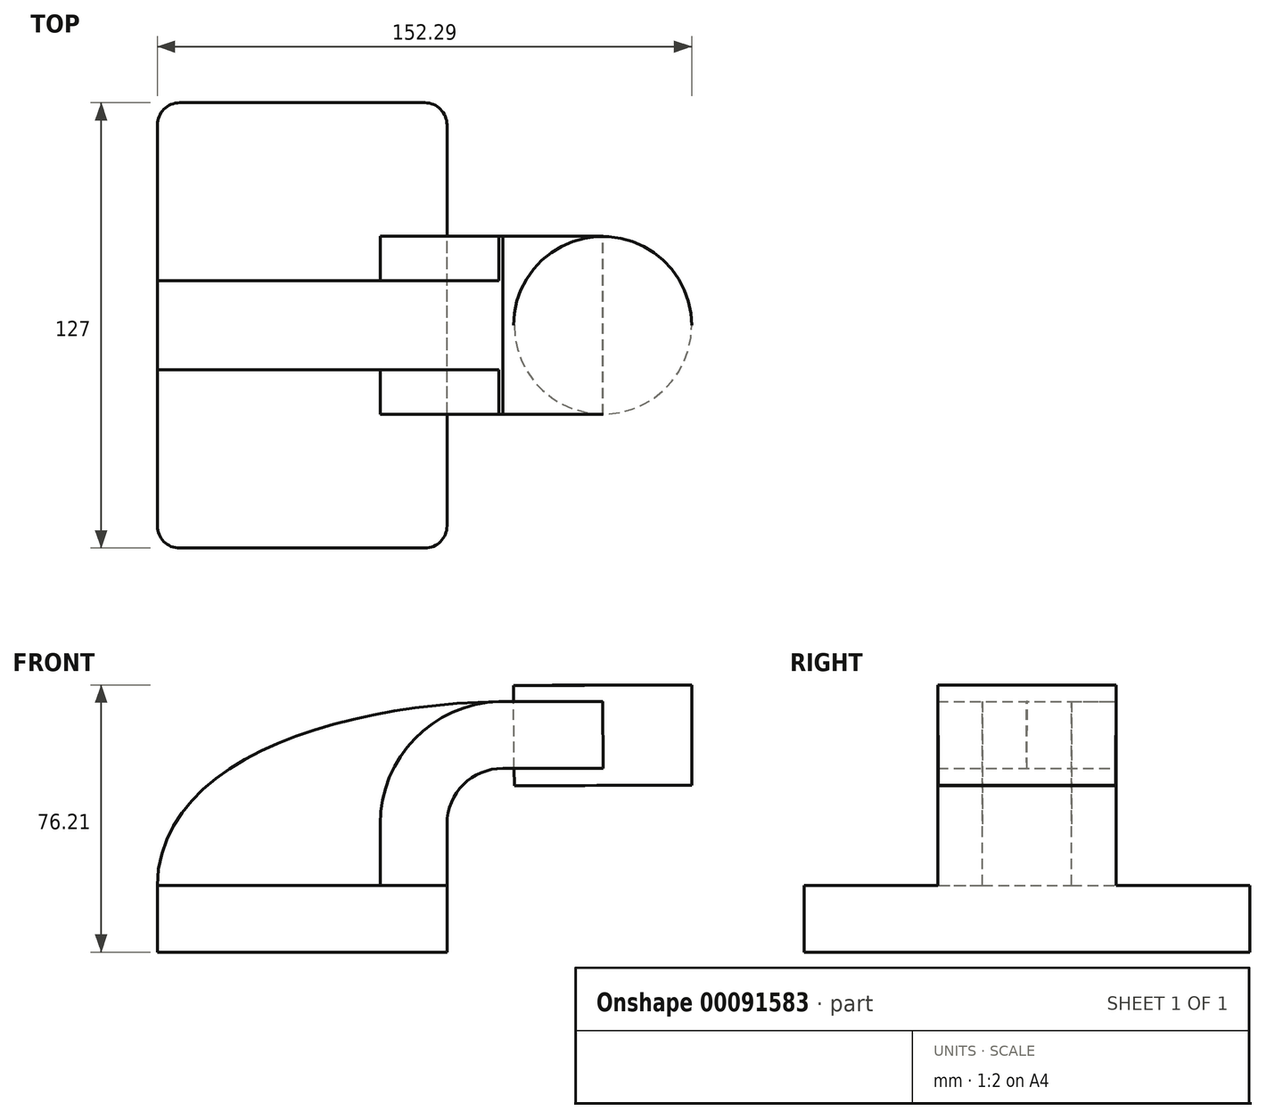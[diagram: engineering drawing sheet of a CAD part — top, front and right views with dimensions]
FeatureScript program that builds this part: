
annotation { "Feature Type Name" : "Feature", "Feature Type Description" : "" }
export const myFeature = defineFeature(function(context is Context, id is Id, definition is map)
    precondition{}
    {
        {
            var Q0;
            Q0=qCreatedBy(makeId("Front.planeOp"),FACE);
            var sketch = newSketch(context, id + "F0", { "sketchPlane" : qUnion([Q0])});
            skLineSegment(sketch, "E0.bottom", {"start": v(41.28, -9.52) * mm, "end": v(-41.27, -9.52) * mm});
            skLineSegment(sketch, "E0.top", {"start": v(41.27, 9.53) * mm, "end": v(-41.28, 9.53) * mm});
            skLineSegment(sketch, "E0.left", {"start": v(41.28, -9.52) * mm, "end": v(41.28, 9.53) * mm});
            skLineSegment(sketch, "E0.right", {"start": v(-41.27, -9.52) * mm, "end": v(-41.28, 9.53) * mm});
            skPoint(sketch, "E0.middle", {"position": v(0, 0) * mm});
            skLineSegment(sketch, "E1.bottom", {"start": v(111.01, 38.1) * mm, "end": v(60.21, 38.1) * mm});
            skLineSegment(sketch, "E1.top", {"start": v(111.01, 66.68) * mm, "end": v(60.21, 66.68) * mm});
            skLineSegment(sketch, "E1.left", {"start": v(111.01, 38.1) * mm, "end": v(111.01, 66.67) * mm});
            skLineSegment(sketch, "E1.right", {"start": v(60.21, 38.1) * mm, "end": v(60.21, 66.67) * mm});
            skPoint(sketch, "E1.middle", {"position": v(85.61, 52.39) * mm});
            skLineSegment(sketch, "E2", {"start": v(41.27, 9.53) * mm, "end": v(41.27, 27) * mm});
            skArc(sketch, "E3", {"start": v(41.27, 27) * mm, "mid": v(45.92, 38.23) * mm, "end": v(57.15, 42.88) * mm});
            skLineSegment(sketch, "E4", {"start": v(57.15, 42.88) * mm, "end": v(85.72, 42.88) * mm});
            skLineSegment(sketch, "E5.0", {"start": v(57.15, 61.93) * mm, "end": v(85.77, 61.93) * mm});
            skArc(sketch, "E5.1", {"start": v(22.23, 27) * mm, "mid": v(32.45, 51.7) * mm, "end": v(57.15, 61.93) * mm});
            skLineSegment(sketch, "E5.2", {"start": v(22.22, 9.53) * mm, "end": v(22.22, 27) * mm});
            skFitSpline(sketch, "E6", {"points": [v(-41.28, 9.53) * mm, v(57.15, 61.93) * mm], "startDerivative": vector(1.5, 109.08) * mm, "endDerivative": vector(136.45, 1.82) * mm});
            skLineSegment(sketch, "E7", {"start": v(85.77, 61.93) * mm, "end": v(85.72, 42.88) * mm});
            skLineSegment(sketch, "E8", {"start": v(85.61, 66.68) * mm, "end": v(85.72, 38.1) * mm});
            skSolve(sketch);
        }
        {
            var Q0;
            Q0=makeQuery(id+"F0.imprint","IMPRINT",FACE,{"disambiguationData":[TD([[makeQuery(id+"F0.imprint","IMPRINT",EDGE,{"derivedFrom":sQuery(id+"F0.wireOp",EDGE,"E0.bottom")}),-1.0]])]});
            extrude(context, id + "F1", {"entities" : qUnion([Q0]), "endBound" : BoundingType.SYMMETRIC, "depth" : 127 * mm});
        }
        {
            var Q0;
            {var subQ1=sQuery(id+"F0.wireOp",EDGE,"E2");Q0=makeQuery(id+"F0.imprint","IMPRINT",FACE,{"disambiguationData":[TD([[makeQuery(id+"F0.imprint","IMPRINT",EDGE,{"derivedFrom":subQ1}),1.0]])]});}
            var Q1;
            {var subQ0=sQuery(id+"F0.wireOp",EDGE,"E4");var subQ1=sQuery(id+"F0.wireOp",EDGE,"E1.right");var subQ2=makeQuery(id+"F0.imprint","INTERSECT",VERTEX,{"derivedFrom":[subQ1,subQ0]});Q1=makeQuery(id+"F0.imprint","IMPRINT",FACE,{"disambiguationData":[TD([[makeQuery(id+"F0.imprint","IMPRINT",EDGE,{"disambiguationData":[TD([[subQ2,-1.0]])],"derivedFrom":subQ1}),-1.0]])]});}
            extrude(context, id + "F2", {"entities" : qUnion([Q0, Q1]), "operationType" : NewBodyOperationType.ADD, "endBound" : BoundingType.SYMMETRIC, "depth" : 50.8 * mm});
        }
        {
            var Q0;
            {var subQ3=sQuery(id+"F0.wireOp",EDGE,"E5.2");Q0=makeQuery(id+"F0.imprint","IMPRINT",FACE,{"disambiguationData":[TD([[makeQuery(id+"F0.imprint","IMPRINT",EDGE,{"derivedFrom":subQ3}),1.0]])]});}
            extrude(context, id + "F3", {"entities" : qUnion([Q0]), "operationType" : NewBodyOperationType.ADD, "endBound" : BoundingType.SYMMETRIC, "depth" : 25.4 * mm});
        }
        {
            var Q0;
            {var subQ4=sQuery(id+"F0.wireOp",EDGE,"E1.left");Q0=makeQuery(id+"F0.imprint","IMPRINT",FACE,{"disambiguationData":[TD([[makeQuery(id+"F0.imprint","IMPRINT",EDGE,{"derivedFrom":subQ4}),1.0]])]});}
            var Q1;
            Q1=sQuery(id+"F0.wireOp",EDGE,"E8");
            revolve(context, id + "F4", {"entities" : qUnion([Q0]), "axis" : qUnion([Q1]), "revolveType" : RevolveType.FULL});
        }
        {
            var Q0;
            Q0=makeQuery(id+"F1.opExtrude","CAP_EDGE",EDGE,{"disambiguationData":[OSD([sQuery(id+"F0.wireOp",EDGE,"E0.left")])],"isStart":false});
            var Q1;
            Q1=makeQuery(id+"F1.opExtrude","CAP_EDGE",EDGE,{"disambiguationData":[OSD([sQuery(id+"F0.wireOp",EDGE,"E0.right")])],"isStart":false});
            var Q2;
            Q2=makeQuery(id+"F1.opExtrude","CAP_EDGE",EDGE,{"disambiguationData":[OSD([sQuery(id+"F0.wireOp",EDGE,"E0.left")])],"isStart":true});
            var Q3;
            Q3=makeQuery(id+"F1.opExtrude","CAP_EDGE",EDGE,{"disambiguationData":[OSD([sQuery(id+"F0.wireOp",EDGE,"E0.right")])],"isStart":true});
            fillet(context, id + "F5", {"entities" : qUnion([Q0, Q1, Q2, Q3]), "radius" : 6.35 * mm, "tangentPropagation" : true, "allowEdgeOverflow" : false});
        }
    });
